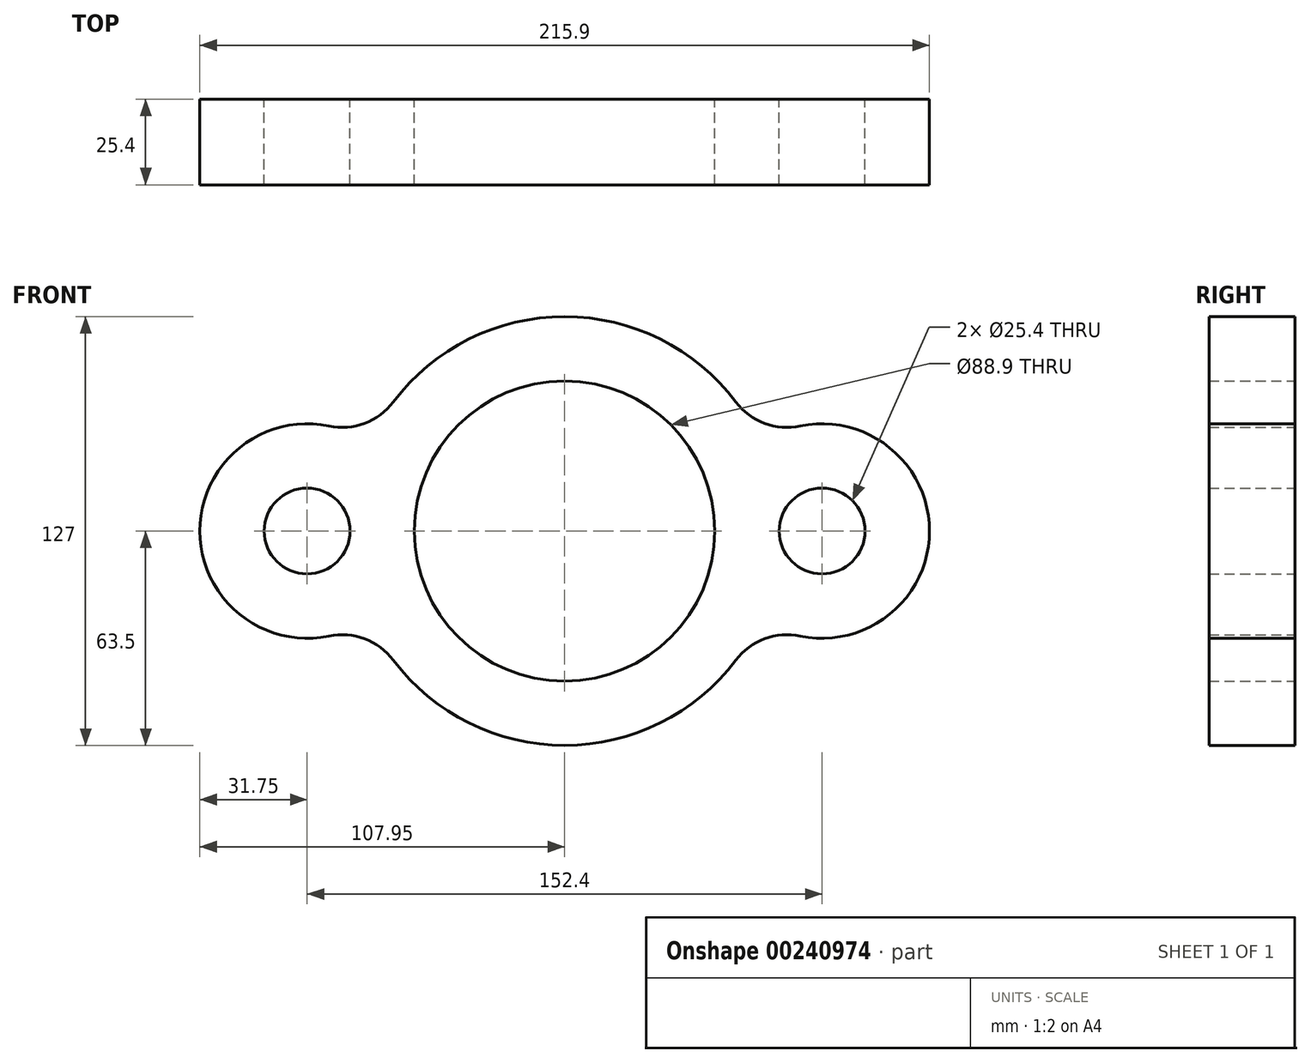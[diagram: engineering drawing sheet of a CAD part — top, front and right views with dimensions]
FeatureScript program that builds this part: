
annotation { "Feature Type Name" : "Feature", "Feature Type Description" : "" }
export const myFeature = defineFeature(function(context is Context, id is Id, definition is map)
    precondition{}
    {
        {
            var Q0;
            Q0=qCreatedBy(makeId("Front.planeOp"),FACE);
            var sketch = newSketch(context, id + "F0", { "sketchPlane" : qUnion([Q0])});
            skArc(sketch, "E0", {"start": v(-50.68, -38.26) * mm, "mid": v(0, -63.5) * mm, "end": v(50.68, -38.26) * mm});
            skCircle(sketch, "E1", {"center": v(0, 0) * mm, "radius": 44.45 * mm});
            skLineSegment(sketch, "E2", {"start": v(-63.5, 0) * mm, "end": v(-76.2, 0) * mm});
            skLineSegment(sketch, "E3", {"start": v(63.5, 0) * mm, "end": v(76.2, 0) * mm});
            skCircle(sketch, "E4", {"center": v(-76.2, 0) * mm, "radius": 12.7 * mm});
            skCircle(sketch, "E5", {"center": v(76.2, 0) * mm, "radius": 12.7 * mm});
            skArc(sketch, "E6", {"start": v(-69.75, 31.09) * mm, "mid": v(-107.95, 0) * mm, "end": v(-69.75, -31.09) * mm});
            skArc(sketch, "E7", {"start": v(69.75, -31.09) * mm, "mid": v(107.95, 0) * mm, "end": v(69.75, 31.09) * mm});
            skArc(sketch, "E8.trimOffspring", {"start": v(50.68, 38.26) * mm, "mid": v(0, 63.5) * mm, "end": v(-50.68, 38.26) * mm});
            skPoint(sketch, "E9.start.orphan", {"position": v(-77.15, -31.74) * mm});
            skPoint(sketch, "E10.start.orphan", {"position": v(88.58, 29.24) * mm});
            skPoint(sketch, "E11.end.orphan", {"position": v(-89.5, 28.83) * mm});
            skPoint(sketch, "E12", {"position": v(-161.02, 52.7) * mm});
            skPoint(sketch, "E13", {"position": v(107.35, 52.7) * mm});
            skPoint(sketch, "E14", {"position": v(57.94, 25.98) * mm});
            skArc(sketch, "E15", {"start": v(-69.75, 31.09) * mm, "mid": v(-59.17, 31.91) * mm, "end": v(-50.68, 38.26) * mm});
            skArc(sketch, "E16", {"start": v(50.68, 38.26) * mm, "mid": v(59.17, 31.91) * mm, "end": v(69.75, 31.09) * mm});
            skArc(sketch, "E17", {"start": v(-50.68, -38.26) * mm, "mid": v(-59.17, -31.91) * mm, "end": v(-69.75, -31.09) * mm});
            skArc(sketch, "E18", {"start": v(69.75, -31.09) * mm, "mid": v(59.17, -31.91) * mm, "end": v(50.68, -38.26) * mm});
            skSolve(sketch);
        }
        {
            var Q0;
            Q0=makeQuery(id+"F0.imprint","IMPRINT",FACE,{"disambiguationData":[TD([[makeQuery(id+"F0.imprint","IMPRINT",EDGE,{"derivedFrom":sQuery(id+"F0.wireOp",EDGE,"E0")}),1.0]])]});
            extrude(context, id + "F1", {"entities" : qUnion([Q0]), "depth" : 25.4 * mm});
        }
        {
            var Q0;
            Q0 = qSketchRegion(id + "F0", true);
            extrude(context, id + "F2", {"entities" : qUnion([Q0]), "operationType" : NewBodyOperationType.ADD, "depth" : 25.4 * mm});
        }
        {
            var Q0;
            Q0=makeQuery(id+"F0.imprint","IMPRINT",FACE,{"disambiguationData":[TD([[makeQuery(id+"F0.imprint","IMPRINT",EDGE,{"derivedFrom":sQuery(id+"F0.wireOp",EDGE,"E1")}),1.0]])]});
            extrude(context, id + "F3", {"entities" : qUnion([Q0]), "operationType" : NewBodyOperationType.REMOVE, "oppositeDirection" : true, "depth" : 25.4 * mm});
        }
    });
